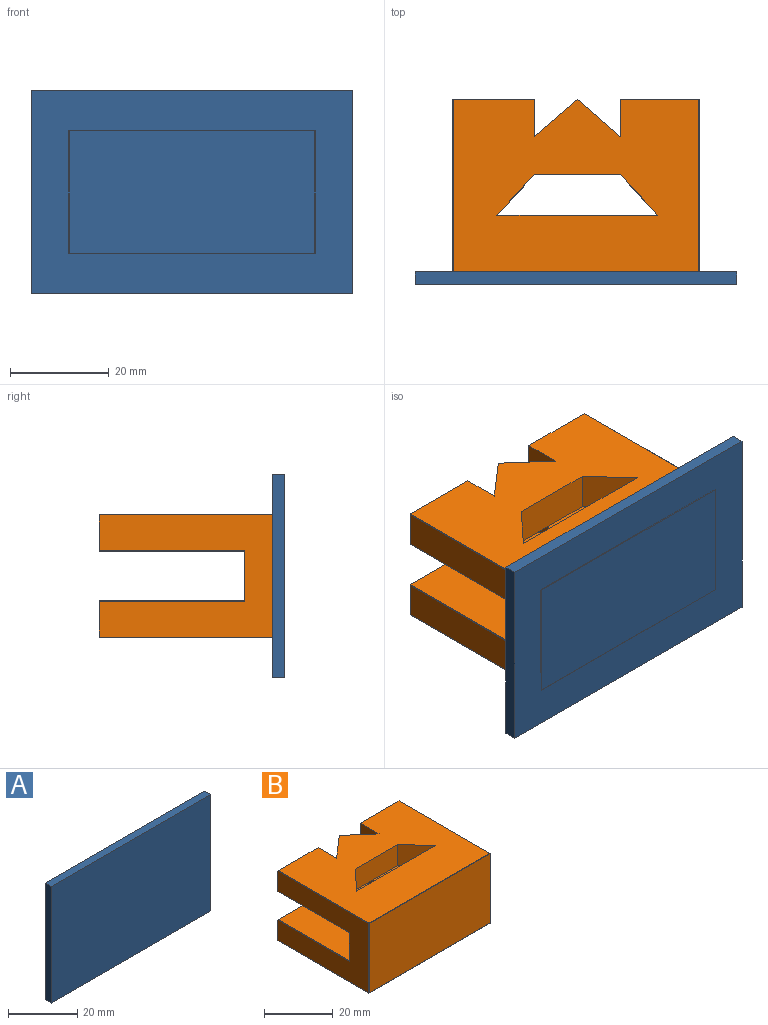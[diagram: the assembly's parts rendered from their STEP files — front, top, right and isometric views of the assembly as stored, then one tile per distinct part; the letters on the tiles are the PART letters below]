
ASSEMBLY  parts=2 mates=1
PART A: 6 faces, bbox 65x2.5x41.1 mm
  f0: plane 41.11x2.54mm, normal (-1,0,0), area 104.4mm2, adj f1,f3,f4,f5
  f1: plane 65.01x2.54mm, normal (0,0,-1), area 165.1mm2, adj f0,f2,f4,f5
  f2: plane 41.11x2.54mm, normal (1,0,0), area 104.4mm2, adj f1,f3,f4,f5
  f3: plane 65.01x2.54mm, normal (0,0,1), area 165.1mm2, adj f0,f2,f4,f5
  f4: plane 65.01x41.11mm, normal (0,-1,0), area 2672.6mm2, adj f0,f1,f2,f3
  f5: plane 65.01x41.11mm, normal (0,1,0), area 2672.6mm2, adj f0,f1,f2,f3
PART B: 46 faces, bbox 50x37.5x25 mm
  f0: plane 49.75x37.37mm, normal (0,0,1), area 1587.9mm2, adj f5,f10,f12,f13,f14,f15,f16,f17
  f1: plane 49.75x37.37mm, normal (0,0,-1), area 1587.9mm2, adj f4,f6,f18,f19,f20,f21,f22,f23
  f2: plane 49.75x29.32mm, normal (0,0,1), area 1187.5mm2, adj f4,f6,f11,f18,f19,f20,f21,f22
  f3: plane 49.75x29.32mm, normal (0,0,-1), area 1187.5mm2, adj f5,f10,f11,f12,f13,f14,f15,f16
  f4: plane 16.56x7.5mm, normal (0,1,0), area 124.2mm2, adj f1,f2,f8,f19,f29,f39
  f5: plane 16.56x7.5mm, normal (0,1,0), area 124.2mm2, adj f0,f3,f8,f12,f28,f45
  f6: plane 16.01x7.5mm, normal (0,1,0), area 120mm2, adj f1,f2,f7,f27,f31,f34
  f7: plane 37.37x24.75mm, normal (1,0,0), area 622.8mm2, adj f6,f10,f31,f32,f33,f34,f36,f37
  f8: plane 37.37x24.75mm, normal (-1,0,0), area 622.8mm2, adj f4,f5,f28,f29,f30,f39,f43,f45
  f9: plane 49.75x24.75mm, normal (0,-1,0), area 1231mm2, adj f37,f38,f42,f43
  f10: plane 16.01x7.5mm, normal (0,1,0), area 120mm2, adj f0,f3,f7,f24,f32,f36
  f11: plane 49.75x10mm, normal (0,1,0), area 497.5mm2, adj f2,f3,f30,f33
  f12: plane 7.55x7.5mm, normal (1,0,0), area 56.6mm2, adj f0,f3,f5,f13
  f13: plane 8.72x7.55mm, normal (-0.65,0.76,0), area 86.5mm2, adj f0,f3,f12,f25
  f14: plane 32.57x7.5mm, normal (0,1,0), area 244.3mm2, adj f0,f3,f15,f17
  f15: plane 8.2x7.57mm, normal (0.73,-0.68,0), area 83.7mm2, adj f0,f3,f14,f16
  f16: plane 17.44x7.5mm, normal (0,-1,0), area 130.8mm2, adj f0,f3,f15,f17
  f17: plane 8.2x7.57mm, normal (-0.73,-0.68,0), area 83.7mm2, adj f0,f3,f14,f16
  f18: plane 8.72x7.55mm, normal (-0.65,0.76,0), area 86.5mm2, adj f1,f2,f19,f26
  f19: plane 7.55x7.5mm, normal (1,0,0), area 56.6mm2, adj f1,f2,f4,f18
  f20: plane 8.2x7.57mm, normal (-0.73,-0.68,0), area 83.7mm2, adj f1,f2,f21,f23
  f21: plane 17.44x7.5mm, normal (0,-1,0), area 130.8mm2, adj f1,f2,f20,f22
  f22: plane 8.2x7.57mm, normal (0.73,-0.68,0), area 83.7mm2, adj f1,f2,f21,f23
  f23: plane 32.57x7.5mm, normal (0,1,0), area 244.3mm2, adj f1,f2,f20,f22
  f24: plane 7.64x7.5mm, normal (-1,0,0), area 57.3mm2, adj f0,f3,f10,f25
  f25: plane 8.72x7.64mm, normal (0.66,0.75,0), area 86.9mm2, adj f0,f3,f13,f24
  f26: plane 8.72x7.64mm, normal (0.66,0.75,0), area 86.9mm2, adj f1,f2,f18,f27
  f27: plane 7.64x7.5mm, normal (-1,0,0), area 57.3mm2, adj f1,f2,f6,f26
  f28: plane 29.45x0.13mm, normal (-0.71,0,-0.71), area 5.3mm2, adj f3,f5,f8,f30
  f29: plane 29.45x0.13mm, normal (-0.71,0,0.71), area 5.3mm2, adj f2,f4,f8,f30
  f30: plane 10.25x0.13mm, normal (-0.71,0.71,0), area 1.8mm2, adj f8,f11,f28,f29
  f31: plane 29.45x0.13mm, normal (0.71,0,0.71), area 5.3mm2, adj f2,f6,f7,f33
  f32: plane 29.45x0.13mm, normal (0.71,0,-0.71), area 5.3mm2, adj f3,f7,f10,f33
  f33: plane 10.25x0.13mm, normal (0.71,0.71,0), area 1.8mm2, adj f7,f11,f31,f32
  f34: plane 37.37x0.13mm, normal (0.71,0,-0.71), area 6.7mm2, adj f1,f6,f7,f35
  f35: plane 0.13x0.13mm, normal (0.58,-0.58,-0.58), area 0mm2, adj f34,f37,f38
  f36: plane 37.37x0.13mm, normal (0.71,0,0.71), area 6.7mm2, adj f0,f7,f10,f40
  f37: plane 24.75x0.13mm, normal (0.71,-0.71,0), area 4.4mm2, adj f7,f9,f35,f40
  f38: plane 49.75x0.13mm, normal (0,-0.71,-0.71), area 8.9mm2, adj f1,f9,f35,f41
  f39: plane 37.37x0.13mm, normal (-0.71,0,-0.71), area 6.7mm2, adj f1,f4,f8,f41
  f40: plane 0.13x0.13mm, normal (0.58,-0.58,0.58), area 0mm2, adj f36,f37,f42
  f41: plane 0.13x0.13mm, normal (-0.58,-0.58,-0.58), area 0mm2, adj f38,f39,f43
  f42: plane 49.75x0.13mm, normal (0,-0.71,0.71), area 8.9mm2, adj f0,f9,f40,f44
  f43: plane 24.75x0.13mm, normal (-0.71,-0.71,0), area 4.4mm2, adj f8,f9,f41,f44
  f44: plane 0.13x0.13mm, normal (-0.58,-0.58,0.58), area 0mm2, adj f42,f43,f45
  f45: plane 37.37x0.13mm, normal (-0.71,0,0.71), area 6.7mm2, adj f0,f5,f8,f44
PLACE A t=(44.56,17.14,-8.09)mm
PLACE B t=(-16.26,52.1,28.73)mm
MATE fastened B.f9 <-> A.f4  axis (0,-1,0) through (8.74,14.6,16.23)mm
